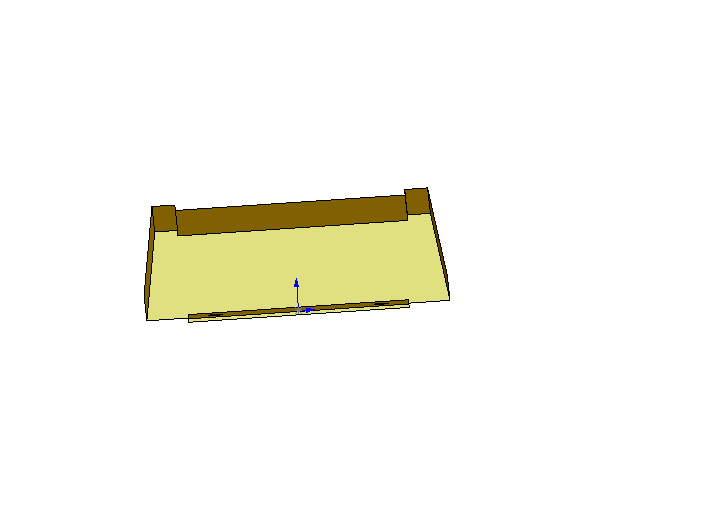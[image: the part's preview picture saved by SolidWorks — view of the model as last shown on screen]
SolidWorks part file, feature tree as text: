
SOLIDWORKS PART (.sldprt)
format: sldprt  version: not decoded by parser v0  size: 130,560 bytes
history: native  units: mm
features: sketch x5, extrude x3, hole x1 (+10 scaffold rows collapsed)
feature tree (19):
  scaffold x10  (default folders/planes/origin — collapsed)
  sketch  "Sketch1"  dims[D1=40.64mm D2=139.7mm D3=6.35mm D4=2.54mm]
  extrude  "Extrude1"  Depth=152.4mm
  sketch  "Sketch2"  dims[D1=101.6mm D2=1.5748mm]
  extrude  "Extrude2"  Depth=25.4mm
  sketch  "Sketch3"  dims[D1=0.0mm]
  extrude  "Extrude3"  Depth=25.4mm
  hole  "1/4 Clearance Hole1"  Diameter=6.5278mm Depth=1.5748mm
  sketch  "Sketch5"  dims[D1=177.8mm D2=76.2mm]
  sketch  "Sketch4"  dims[hole-wizard template sketch: 60 standard entries collapsed; hole parameters kept: c18.Thru Hole Depth=1.5748mm]
decode coverage: 9 of 9 modeling features carry decoded parameters
note: ~ marks probable driven/reference dimensions
note: suppression state not decoded; provenance and decode notes live in map.json
